MODEL satellite_behaviour_with_control
KIND model
CONFIG PreLoadFcn = \n
CONFIG StartFcn = \n\n
BLOCK [Constant] Constant
  Value = [4.5 4.5 4.5]*1e-5
BLOCK [Constant] Constant1
  Value = [0.6 0 0.8 0]
BLOCK [Demux] Demux
  DisplayOption = bar
  Ports = [1, 4]
BLOCK [DigitalClock] Digital Clock
BLOCK [Display] Display
  Decimation = 1
  Lockdown = off
  Ports = [1]
BLOCK [Display] Display1
  Decimation = 1
  Lockdown = off
  Ports = [1]
BLOCK [Display] Display2
  Decimation = 1
  Format = long
  Lockdown = off
  Ports = [1]
BLOCK [Scope] Euler angles
  DataFormat = StructureWithTime
  Floating = off
  LimitDataPoints = off
  NumInputPorts = 1
  Ports = [1]
  SampleTime = 0
  SaveName = ScopeData1
  YMax = 3.5
  YMin = -3.5
BLOCK [From] From
  CloseFcn = tagdialog Close
  GotoTag = Sim_time_JD
BLOCK [From] From1
  CloseFcn = tagdialog Close
  GotoTag = Omega_S
BLOCK [From] From16
  CloseFcn = tagdialog Close
  GotoTag = Eclipse
BLOCK [From] From2
  CloseFcn = tagdialog Close
  GotoTag = Omega_S
BLOCK [From] From3
  CloseFcn = tagdialog Close
  GotoTag = q_I_S
BLOCK [From] From8
  CloseFcn = tagdialog Close
  GotoTag = q_I_S
BLOCK [Gain] Gain
  Gain = K
  Multiplication = Matrix(K*u)
  OutDataTypeMode = Inherit via internal rule
  ParameterDataTypeMode = Inherit via internal rule
  SaturateOnIntegerOverflow = off
BLOCK [Gain] Gain1
  Gain = 2
  OutDataTypeMode = Inherit via internal rule
  ParameterDataTypeMode = Inherit via internal rule
  SaturateOnIntegerOverflow = off
BLOCK [Reference] Model Info  REF=simulink/Model-Wide\nUtilities/Model Info
  BlockCM = None
  DisplayStringWithTags = sun to eclipse : 2452315.560376\n32 sec. before : 2452315.56\neclipse to sun : 2452315.513363
  Frame = on
  HorizontalTextAlignment = Center
  InitialBlockCM = None
  LeftAlignmentValue = 0.5
  MaskDisplayString = sun to eclipse : 2452315.560376\\n32 sec. before : 2452315.56\\neclipse to sun : 2452315.513363
  Ports = []
  ShowPortLabels = on
  SourceBlock = simulink/Model-Wide\nUtilities/Model Info
  SourceBlockDiagram = satellite_behaviour_with_control
  SourceType = CMBlock
  TagMaxNumber = 20
BLOCK [Mux] Mux
  DisplayOption = bar
  Inputs = 3
  Ports = [3, 1]
BLOCK [Reference] NSO  REF=components_lib/NSO  (lib defined in mdl_419550584dda)
  Cd = 2
  Description = AAUSAT-II Model
  Dim = [0.1 0.1 0.3]
  Ports = [4, 4]
  ShowPortLabels = on
  SourceBlock = components_lib/NSO
  Tag = AAUSAT-II Model
  alb_emu_enabled = off
  enable_dist = off
  enable_sensor_emulation = off
  inertia_c = [25 25 5]/1e3
  inertia_d = [42.3 42.3 28.4]/1e3
  init_jd = 2452315.56
  mass_sc = 3
  q_init_s_i = [sqrt(0.5) 0 0 sqrt(0.5)]
  q_s_c = [0 0 0 1]
  r_com_s = [0.05 0.05 0.15]
  r_com_s_deployed = [0.05 0.05 0.125]
  rho = 9.25e-13
  sat_temp_start = 0
  w_init_s = [0.1 0.1 0.1]
BLOCK [Reference] Quaternion inverter1  REF=components_lib/Math utilities/Quaternion operations/Quaternion inverter  (lib defined in mdl_419550584dda)
  Ports = [1, 1]
  ShowPortLabels = on
  SourceBlock = components_lib/Math utilities/Quaternion operations/Quaternion inverter
  SourceType = SubSystem
BLOCK [Step] Step
  SampleTime = 0
  Time = 0
BLOCK [Sum] Sum
  IconShape = round
  InputSameDT = off
  Inputs = |+-
  OutDataTypeMode = Inherit via internal rule
  Ports = [2, 1]
  SaturateOnIntegerOverflow = off
BLOCK [Terminator] Terminator
BLOCK [Scope] control torque
  DataFormat = StructureWithTime
  Floating = off
  LimitDataPoints = off
  NumInputPorts = 1
  Ports = [1]
  SampleTime = 0
  SaveName = ScopeData6
  YMax = 6e-06
  YMin = -7e-06
  ZoomMode = yonly
BLOCK [Scope] omega and q
  DataFormat = StructureWithTime
  Floating = off
  LimitDataPoints = off
  NumInputPorts = 2
  Ports = [2]
  SampleTime = 0
  YMax = 1.75e-06~0.8
  YMin = -5e-07~-0.05
  ZoomMode = xonly
BLOCK [Scope] omega ref
  DataFormat = StructureWithTime
  Floating = off
  LimitDataPoints = off
  NumInputPorts = 1
  Ports = [1]
  SampleTime = 0
  SaveName = ScopeData2
  YMax = 0.7
  YMin = -1.2
BLOCK [Scope] q_err
  DataFormat = StructureWithTime
  Floating = off
  LimitDataPoints = off
  NumInputPorts = 1
  Ports = [1]
  SampleTime = 0
  SaveName = ScopeData5
  YMax = 1
  YMin = -0.4
BLOCK [Reference] qmul no func  REF=components_lib/Math utilities/Quaternion operations/qmul no func  (lib defined in mdl_419550584dda)
  Ports = [2, 1]
  ShowPortLabels = on
  SourceBlock = components_lib/Math utilities/Quaternion operations/qmul no func
  SourceType = SubSystem
BLOCK [Reference] quaternion2euler  REF=components_lib/Math utilities/Quaternion operations/quaternion2euler  (lib defined in mdl_419550584dda)
  Ports = [1, 1]
  ShowPortLabels = on
  SourceBlock = components_lib/Math utilities/Quaternion operations/quaternion2euler
  SourceType = SubSystem
ANNOTATION (root): 
ANNOTATION (root): Angular velocity and Attitude display
ANNOTATION (root): Simulation Time
LINE Constant1:1 -> qmul no func:2
LINE Constant:1 -> NSO:3
LINE Demux:1 -> Mux:1
LINE Demux:2 -> Mux:2
LINE Demux:3 -> Mux:3
LINE Demux:4 -> Terminator:1
LINE Digital Clock:1 -> Display2:1
LINE From16:1 -> Display1:1
LINE From1:1 -> omega and q:1
LINE From2:1 -> Sum:1
LINE From3:1 -> Quaternion inverter1:1
NET From8:1 -> omega and q:2, quaternion2euler:1
LINE From:1 -> Display:1
NET Gain1:1 -> Sum:2, omega ref:1
NET Gain:1 -> NSO:2, control torque:1
LINE Mux:1 -> Gain1:1
LINE Quaternion inverter1:1 -> qmul no func:1
LINE Step:1 -> NSO:4
LINE Sum:1 -> Gain:1
NET qmul no func:1 -> Demux:1, q_err:1
LINE quaternion2euler:1 -> Euler angles:1
note: NET lines group one-source signal fan-out (src -> all destinations, sorted); 1:1 wires keep LINE
